# Revit family: Bloom Lounge Chair
name_source: partatom
category: Furniture
revit_build: Autodesk Revit 2017 (Build: 20160225_1515(x64)
units: mm (PartAtom-declared; Revit-internal decimal feet)

## family parameters
Always vertical = Yes
Cut with Voids When Loaded = No
OmniClass Number = 23.40.20.00
OmniClass Title = General Furniture and Specialties
Room Calculation Point = No
Shared = No
Work Plane-Based = No

## types (1)
- Bloom Lounge Chair
    Armrest height = 25 mm  [stored 0.082021 ft]
    Assembly Code = E2020200
    Assistance = Call for assistance number: 336.941.3446
    Chair type = Lounge
    Collection = Bloom
    Depth = 33 mm  [stored 0.108268 ft]
    Description = Chair fully upholstered with wood legs
    Height = 34 mm
    Industry = Lounge, Hotel, Club, College
    Length = 27 mm  [stored 0.0885827 ft]
    Manufacturer = Beaufurn
    Manufacturer Country = USA
    Model = Bloom Lounge Chair
    Products of collection = Bloom Arm Chair, Bloom Side Chair and Bloom Barstools
    Seat depth = 24 mm
    Seat height = 18 mm  [stored 0.0590551 ft]
    Structure material = Standard wood finishes or Cof
    Type Comments = Lounge Chair ideal for Colleges, Hotels and Universities
    URL = http://beaufurn.com
    Upholstery material = Graded Fabric or Com
    Usage = Indoor
    Yardage = 4 mm  [stored 0.0131234 ft]

note: [stored X ft] marks values corroborated as IEEE doubles in the binary element streams (Revit-internal decimal feet)

## geometry (parser evidence)
native form markers: Sweep x2
no freeform markers — native parametric forms only
